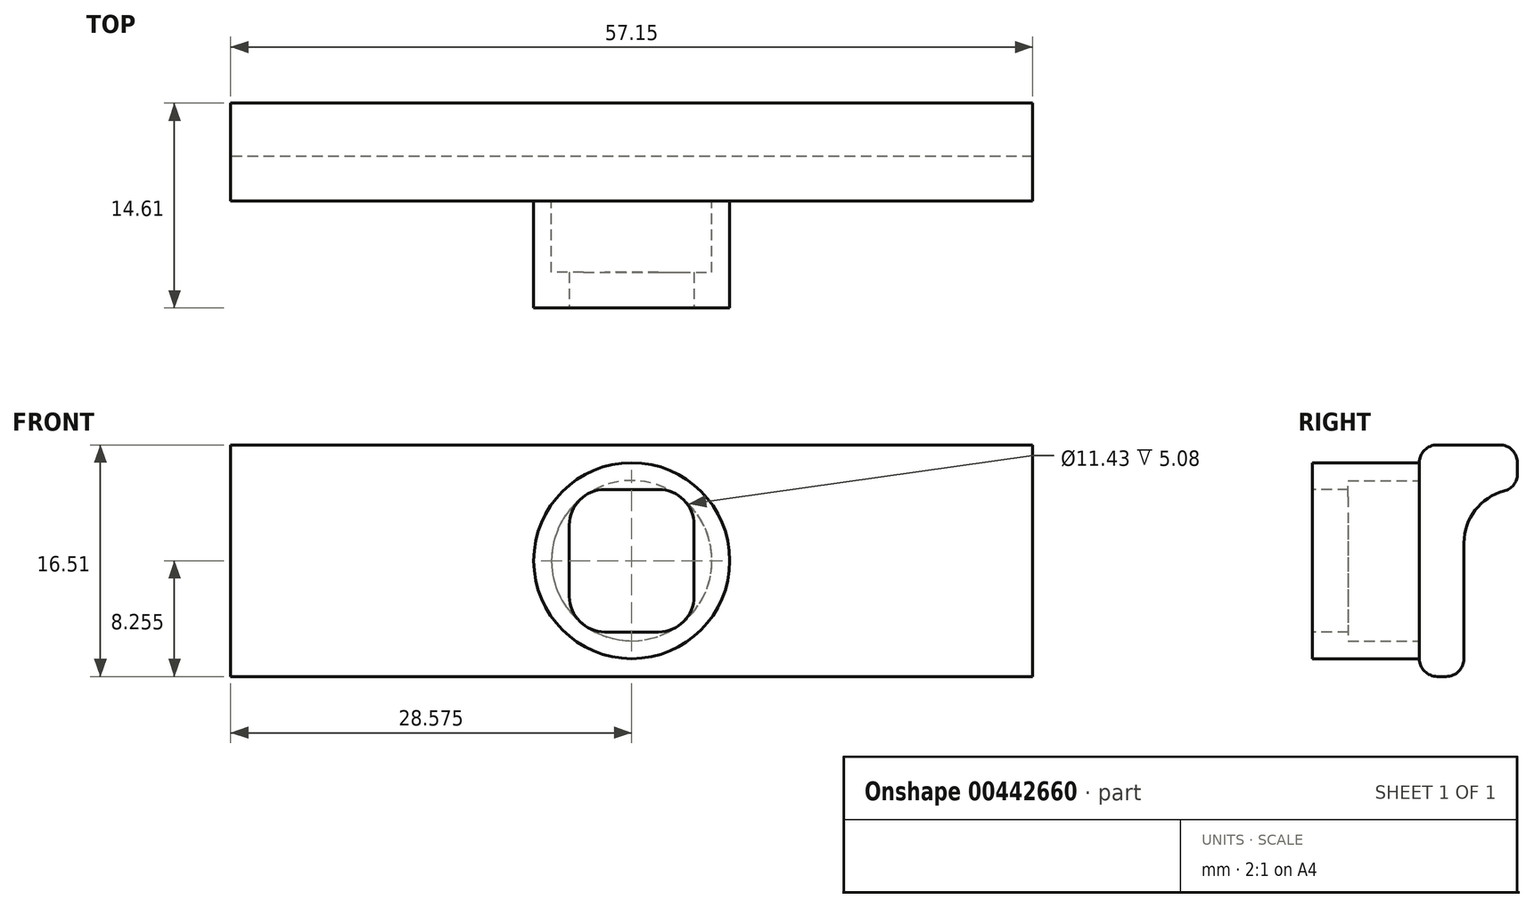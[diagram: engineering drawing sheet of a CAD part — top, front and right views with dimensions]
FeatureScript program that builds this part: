
annotation { "Feature Type Name" : "Feature", "Feature Type Description" : "" }
export const myFeature = defineFeature(function(context is Context, id is Id, definition is map)
    precondition{}
    {
        {
            var Q0;
            Q0=qCreatedBy(makeId("Right.planeOp"),FACE);
            var sketch = newSketch(context, id + "F0", { "sketchPlane" : qUnion([Q0])});
            skLineSegment(sketch, "E0", {"start": v(0, 1.27) * mm, "end": v(0, 10.16) * mm});
            skLineSegment(sketch, "E1", {"start": v(1.27, 0) * mm, "end": v(1.9, 0) * mm});
            skLineSegment(sketch, "E2", {"start": v(6.99, 15.24) * mm, "end": v(6.99, 14.44) * mm});
            skLineSegment(sketch, "E3", {"start": v(0, 10.16) * mm, "end": v(0, 15.24) * mm});
            skPoint(sketch, "E4.orphan", {"position": v(8.34, 13.34) * mm});
            skPoint(sketch, "E5.orphan", {"position": v(3.05, 10.16) * mm});
            skLineSegment(sketch, "E6", {"start": v(3.18, 1.27) * mm, "end": v(3.18, 9.53) * mm});
            skPoint(sketch, "E7.end.orphan", {"position": v(2.36, 13.34) * mm});
            skLineSegment(sketch, "E8", {"start": v(6.99, 13.34) * mm, "end": v(6.99, 13.34) * mm});
            skLineSegment(sketch, "E9", {"start": v(1.27, 16.51) * mm, "end": v(5.72, 16.51) * mm});
            skPoint(sketch, "E10.visualSharp", {"position": v(3.17, 13.34) * mm});
            skArc(sketch, "E10.filletArc", {"start": v(6.03, 13.21) * mm, "mid": v(3.97, 11.86) * mm, "end": v(3.17, 9.53) * mm});
            skPoint(sketch, "E11.visualSharp", {"position": v(6.99, 16.51) * mm});
            skArc(sketch, "E11.filletArc", {"start": v(6.99, 15.24) * mm, "mid": v(6.61, 16.14) * mm, "end": v(5.72, 16.51) * mm});
            skPoint(sketch, "E12.visualSharp", {"position": v(0, 16.51) * mm});
            skArc(sketch, "E12.filletArc", {"start": v(1.27, 16.51) * mm, "mid": v(0.37, 16.14) * mm, "end": v(0, 15.24) * mm});
            skPoint(sketch, "E13.visualSharp", {"position": v(3.18, 0) * mm});
            skArc(sketch, "E13.filletArc", {"start": v(1.9, 0) * mm, "mid": v(2.8, 0.37) * mm, "end": v(3.17, 1.27) * mm});
            skPoint(sketch, "E14.visualSharp", {"position": v(0, 0) * mm});
            skArc(sketch, "E14.filletArc", {"start": v(0, 1.27) * mm, "mid": v(0.37, 0.37) * mm, "end": v(1.27, 0) * mm});
            skPoint(sketch, "E15.visualSharp", {"position": v(6.99, 13.34) * mm});
            skArc(sketch, "E15.filletArc", {"start": v(6.03, 13.21) * mm, "mid": v(6.72, 13.67) * mm, "end": v(6.99, 14.44) * mm});
            skSolve(sketch);
        }
        {
            var Q0;
            Q0=makeQuery(id+"F0.imprint","IMPRINT",FACE,{"disambiguationData":[TD([[makeQuery(id+"F0.imprint","IMPRINT",EDGE,{"derivedFrom":sQuery(id+"F0.wireOp",EDGE,"E0")}),-1.0]])]});
            extrude(context, id + "F1", {"entities" : qUnion([Q0]), "depth" : 57.15 * mm});
        }
        {
            var Q0;
            Q0=makeQuery(id+"F1.opExtrude","SWEPT_FACE",FACE,{"disambiguationData":[OSD([sQuery(id+"F0.wireOp",EDGE,"E0"),sQuery(id+"F0.wireOp",EDGE,"E3")])]});
            var sketch = newSketch(context, id + "F2", { "sketchPlane" : qUnion([Q0])});
            skCircle(sketch, "E16", {"center": v(28.58, 8.26) * mm, "radius": 6.99 * mm});
            skCircle(sketch, "E17", {"center": v(28.58, 8.26) * mm, "radius": 5.72 * mm});
            skSolve(sketch);
        }
        {
            var Q0;
            Q0=makeQuery(id+"F2.imprint","IMPRINT",FACE,{"disambiguationData":[TD([[makeQuery(id+"F2.imprint","IMPRINT",EDGE,{"derivedFrom":sQuery(id+"F2.wireOp",EDGE,"E17")}),-1.0]])]});
            extrude(context, id + "F3", {"entities" : qUnion([Q0]), "operationType" : NewBodyOperationType.ADD, "depth" : 5.08 * mm});
        }
        {
            var Q0;
            Q0=makeQuery(id+"F3.opExtrude","CAP_FACE",FACE,{"disambiguationData":[OSD([sQuery(id+"F2.wireOp",EDGE,"E16"),sQuery(id+"F2.wireOp",EDGE,"E17")])],"isStart":false});
            var sketch = newSketch(context, id + "F4", { "sketchPlane" : qUnion([Q0])});
            skPoint(sketch, "E18.first.point", {"position": v(21.85, 6.35) * mm});
            skPoint(sketch, "E18.second.point", {"position": v(21.79, 9.9) * mm});
            skPoint(sketch, "E18.third.point", {"position": v(21.79, 9.9) * mm});
            skCircle(sketch, "E19", {"center": v(28.58, 8.26) * mm, "radius": 6.99 * mm});
            skSolve(sketch);
        }
        {
            var Q0;
            Q0=qSketchRegion(id+"F4",true);
            extrude(context, id + "F5", {"entities" : qUnion([Q0]), "operationType" : NewBodyOperationType.ADD, "depth" : 2.54 * mm});
        }
        {
            var Q0;
            Q0=makeQuery(id+"F5.opExtrude","CAP_FACE",FACE,{"disambiguationData":[OSD([sQuery(id+"F4.wireOp",EDGE,"E19")])],"isStart":false});
            var sketch = newSketch(context, id + "F6", { "sketchPlane" : qUnion([Q0])});
            skLineSegment(sketch, "E20.top", {"start": v(28.58, 13.33) * mm, "end": v(30.48, 13.33) * mm});
            skLineSegment(sketch, "E20.right", {"start": v(33.02, 8.25) * mm, "end": v(33.02, 10.8) * mm});
            skLineSegment(sketch, "E21.bottom", {"start": v(30.48, 13.33) * mm, "end": v(26.67, 13.33) * mm});
            skLineSegment(sketch, "E21.top", {"start": v(30.48, 3.17) * mm, "end": v(26.67, 3.17) * mm});
            skLineSegment(sketch, "E21.left", {"start": v(33.02, 8.25) * mm, "end": v(33.02, 5.71) * mm});
            skLineSegment(sketch, "E21.right", {"start": v(24.13, 10.8) * mm, "end": v(24.13, 5.71) * mm});
            skPoint(sketch, "E22.visualSharp", {"position": v(24.13, 13.33) * mm});
            skArc(sketch, "E22.filletArc", {"start": v(26.67, 13.33) * mm, "mid": v(24.87, 12.6) * mm, "end": v(24.13, 10.8) * mm});
            skPoint(sketch, "E23.visualSharp", {"position": v(24.13, 3.17) * mm});
            skArc(sketch, "E23.filletArc", {"start": v(24.13, 5.71) * mm, "mid": v(24.87, 3.92) * mm, "end": v(26.67, 3.17) * mm});
            skPoint(sketch, "E24.visualSharp", {"position": v(33.02, 3.17) * mm});
            skArc(sketch, "E24.filletArc", {"start": v(30.48, 3.17) * mm, "mid": v(32.28, 3.92) * mm, "end": v(33.02, 5.71) * mm});
            skPoint(sketch, "E25.visualSharp", {"position": v(33.02, 13.33) * mm});
            skArc(sketch, "E25.filletArc", {"start": v(33.02, 10.8) * mm, "mid": v(32.28, 12.6) * mm, "end": v(30.48, 13.33) * mm});
            skPoint(sketch, "E20.bottom.start.orphan", {"position": v(28.58, 8.26) * mm});
            skSolve(sketch);
        }
        {
            var Q0;
            Q0=makeQuery(id+"F6.imprint","IMPRINT",FACE,{"disambiguationData":[TD([[makeQuery(id+"F6.imprint","IMPRINT",EDGE,{"derivedFrom":sQuery(id+"F6.wireOp",EDGE,"E20.right")}),1.0]])]});
            extrude(context, id + "F7", {"entities" : qUnion([Q0]), "operationType" : NewBodyOperationType.REMOVE, "oppositeDirection" : true, "depth" : 5.08 * mm});
        }
    });
